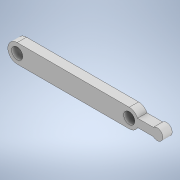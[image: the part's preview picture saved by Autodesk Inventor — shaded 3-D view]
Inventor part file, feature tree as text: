
AUTODESK INVENTOR PART (.ipt)
format: ipt  version: 2022 (Build 260153000, 153)  size: 117,760 bytes
history: native  units: mm
features: extrude x1, sketch x1
ambient origin geometry x8: Origin, YZ Plane, XZ Plane, XY Plane, X Axis, Y Axis, Z Axis, Center Point
bodies: Solid1 (feature_tree)
feature tree (2):
  extrude  "Extrusion1"  Depth=5.0mm
  sketch  "Sketch1"  dims[d0=10.0mm d1=6.0mm d3=60.0mm d4=5.0mm d5=0.0mm d6=15.0mm d7=6.0mm]
